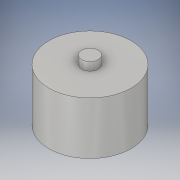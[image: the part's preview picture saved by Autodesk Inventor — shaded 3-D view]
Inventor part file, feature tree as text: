
AUTODESK INVENTOR PART (.ipt)
format: ipt  version: 2018 (Build 220112000, 112)  size: 115,712 bytes
history: native  units: in
note: dims shown in document units (in); Inventor stores cm internally (conversion verified against a paired STEP export)
features: sketch x3, extrude x2, hole x2
ambient origin geometry x8: Origin, YZ Plane, XZ Plane, XY Plane, X Axis, Y Axis, Z Axis, Center Point
bodies: Solid1 (feature_tree)
feature tree (7):
  extrude  "Extrusion1"  Depth=1.2598in TaperAngle=0.0deg
  extrude  "Extrusion2"  Depth=0.1969in TaperAngle=0.0deg
  sketch  "Sketch3"  dims[d6=1.1811in d7=0.3937in d8=0.1969in d9=0.2362in d10=0.1575in d11=0.0787in d12=90.0deg d13=0.3937in d14=0.0in d15=0.315in d16=0.2362in d17=0.1575in d18=0.0787in d19=90.0deg d20=0.3937in d21=0.0in]
  hole  "Hole1"  [1 undecoded]
  hole  "Hole2"  [1 undecoded]
  sketch  "Sketch1"  dims[d0=1.9685in d1=1.2598in d2=0.0in]
  sketch  "Sketch2"  dims[d3=0.3937in d4=0.1969in d5=0.0in]
note: 2 required parameter values undecoded (feature->parameter linkage not recoverable at this tier; creation-order binding heuristic only, values carry confidence <= 0.55)
